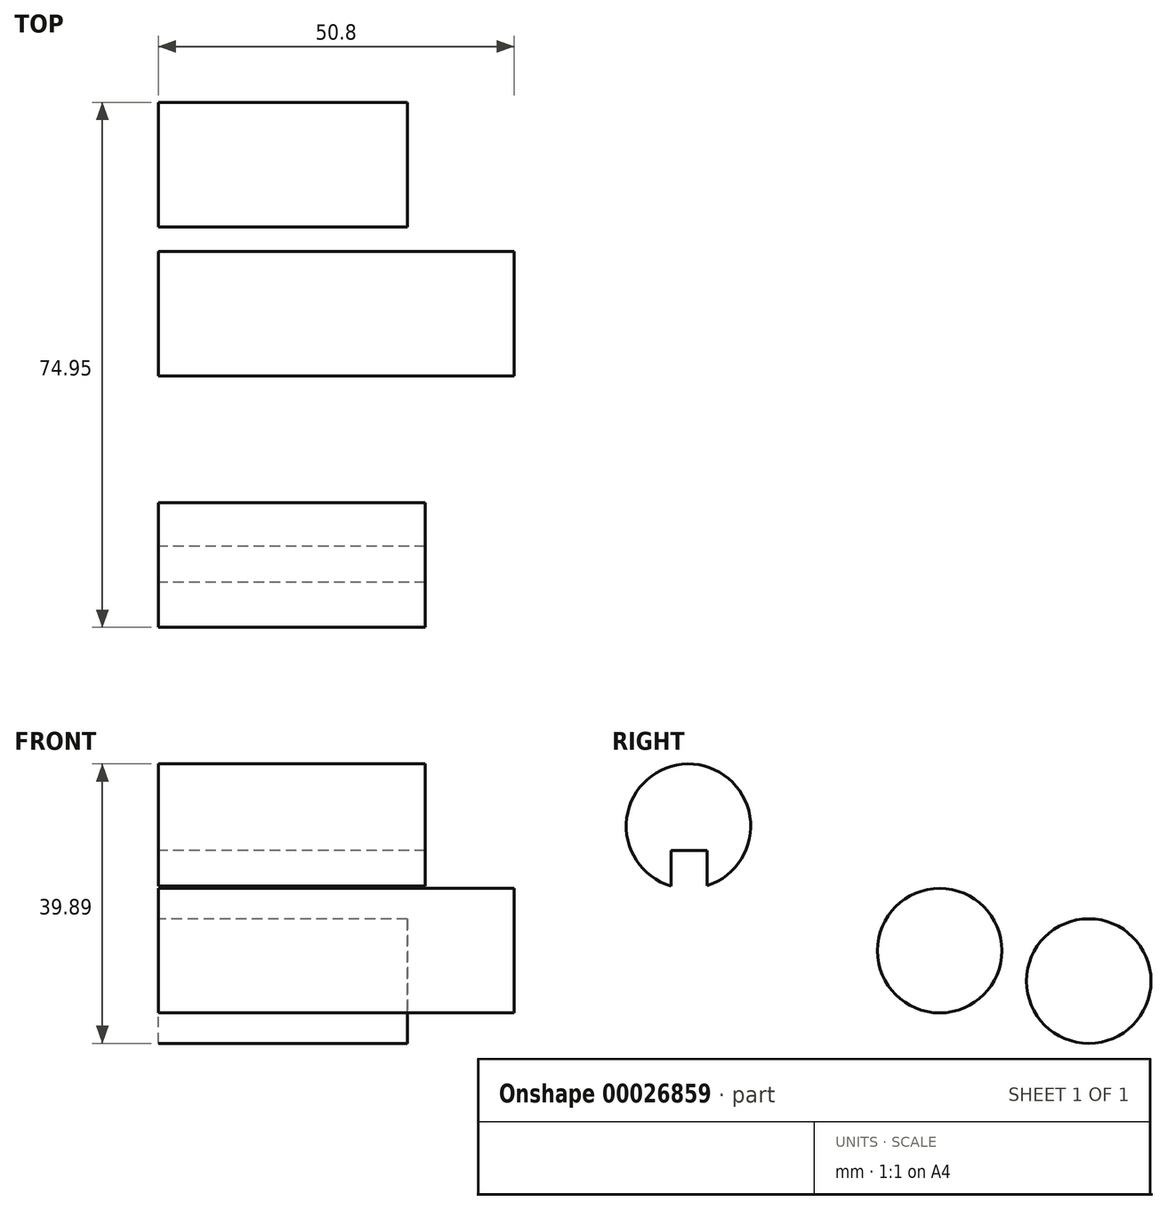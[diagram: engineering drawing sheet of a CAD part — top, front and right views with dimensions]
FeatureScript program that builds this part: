
annotation { "Feature Type Name" : "Feature", "Feature Type Description" : "" }
export const myFeature = defineFeature(function(context is Context, id is Id, definition is map)
    precondition{}
    {
        {
            var Q0;
            Q0=qCreatedBy(makeId("Right.planeOp"),FACE);
            var sketch = newSketch(context, id + "F0", { "sketchPlane" : qUnion([Q0])});
            skCircle(sketch, "E0", {"center": v(-75.1, -6.4) * mm, "radius": 8.9 * mm});
            skSolve(sketch);
        }
        {
            var Q0;
            Q0=makeQuery(id+"F0.imprint","IMPRINT",FACE,{"disambiguationData":[TD([[makeQuery(id+"F0.imprint","IMPRINT",EDGE,{"derivedFrom":sQuery(id+"F0.wireOp",EDGE,"E0")}),1.0]])]});
            extrude(context, id + "F1", {"entities" : qUnion([Q0]), "depth" : 35.56 * mm});
        }
        {
            var Q0;
            Q0=qCreatedBy(makeId("Right.planeOp"),FACE);
            var sketch = newSketch(context, id + "F2", { "sketchPlane" : qUnion([Q0])});
            skCircle(sketch, "E1", {"center": v(-96.38, -2.07) * mm, "radius": 8.9 * mm});
            skSolve(sketch);
        }
        {
            var Q0;
            Q0=makeQuery(id+"F2.imprint","IMPRINT",FACE,{"disambiguationData":[TD([[makeQuery(id+"F2.imprint","IMPRINT",EDGE,{"derivedFrom":sQuery(id+"F2.wireOp",EDGE,"E1")}),1.0]])]});
            extrude(context, id + "F3", {"entities" : qUnion([Q0]), "depth" : 50.8 * mm});
        }
        {
            var Q0;
            Q0=qCreatedBy(makeId("Right.planeOp"),FACE);
            var sketch = newSketch(context, id + "F4", { "sketchPlane" : qUnion([Q0])});
            skArc(sketch, "E2", {"start": v(-129.66, 7.2) * mm, "mid": v(-132.32, 24.6) * mm, "end": v(-134.74, 7.16) * mm});
            skLineSegment(sketch, "E3.rect.left", {"start": v(-129.66, 7.2) * mm, "end": v(-129.66, 9.35) * mm});
            skLineSegment(sketch, "E3.rect.right", {"start": v(-134.74, 7.16) * mm, "end": v(-134.74, 9.35) * mm});
            skPoint(sketch, "E3.rect.middle", {"position": v(-132.2, 6.81) * mm});
            skPoint(sketch, "E4.orphan", {"position": v(-134.74, 4.27) * mm});
            skPoint(sketch, "E5.orphan", {"position": v(-129.66, 4.27) * mm});
            skLineSegment(sketch, "E6.top", {"start": v(-134.74, 12.24) * mm, "end": v(-129.57, 12.24) * mm});
            skLineSegment(sketch, "E6.left", {"start": v(-134.74, 7.16) * mm, "end": v(-134.74, 12.24) * mm});
            skLineSegment(sketch, "E6.right", {"start": v(-129.57, 7.16) * mm, "end": v(-129.57, 12.24) * mm});
            skSolve(sketch);
        }
        {
            var Q0;
            Q0=makeQuery(id+"F4.imprint","IMPRINT",FACE,{"disambiguationData":[TD([[makeQuery(id+"F4.imprint","IMPRINT",EDGE,{"derivedFrom":sQuery(id+"F4.wireOp",EDGE,"E2")}),1.0]])]});
            extrude(context, id + "F5", {"entities" : qUnion([Q0]), "depth" : 38.1 * mm});
        }
    });
